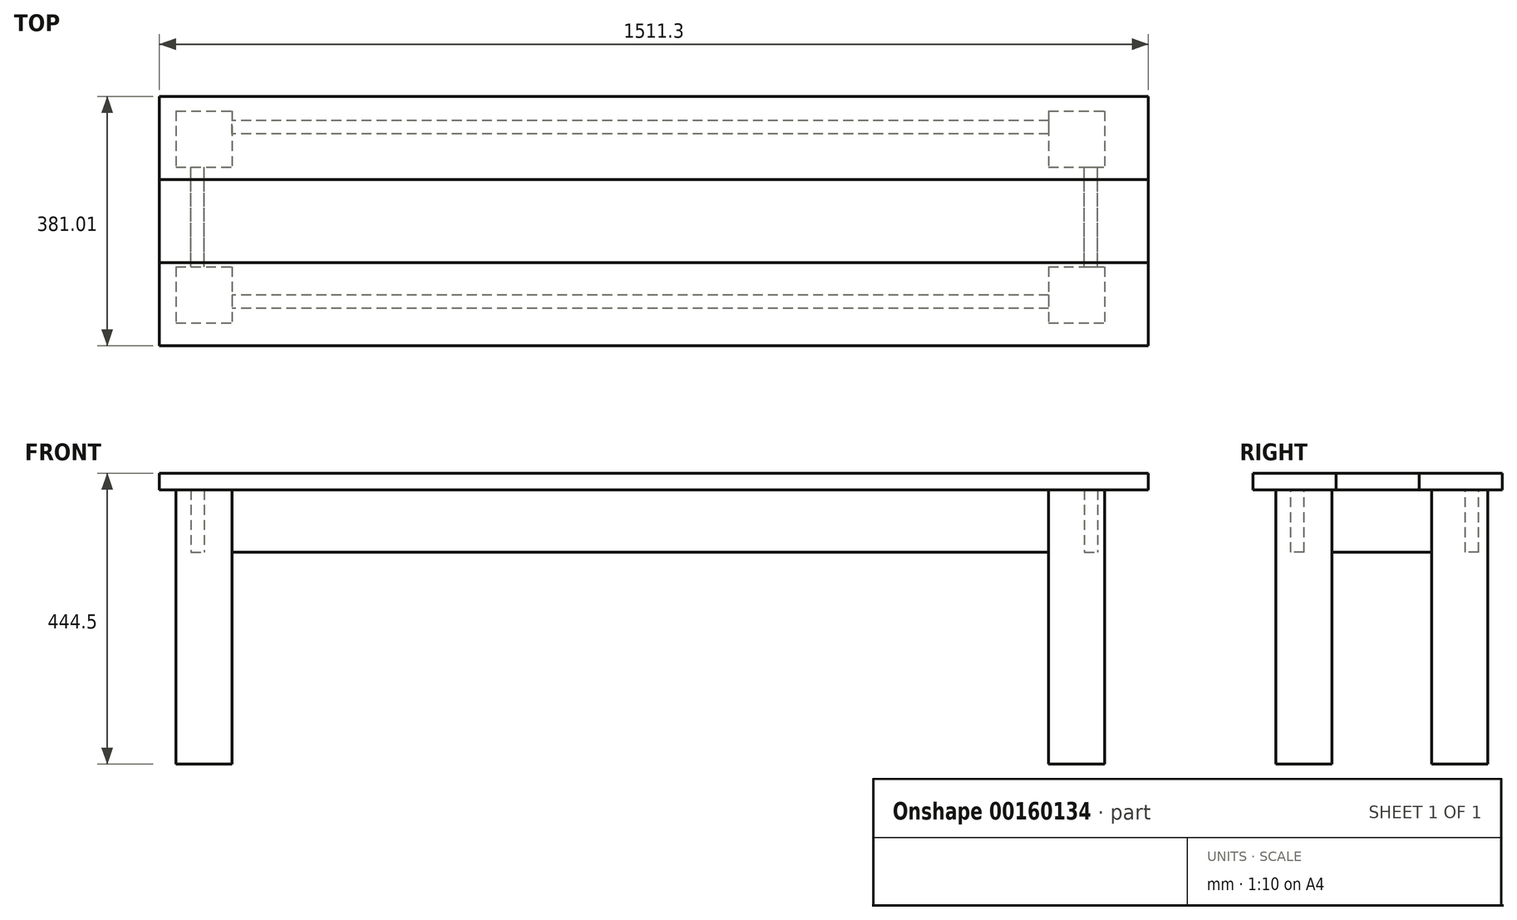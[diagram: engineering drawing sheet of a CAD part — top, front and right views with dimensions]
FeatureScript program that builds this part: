
annotation { "Feature Type Name" : "Feature", "Feature Type Description" : "" }
export const myFeature = defineFeature(function(context is Context, id is Id, definition is map)
    precondition{}
    {
        {
            var Q0;
            Q0=qCreatedBy(makeId("Top.planeOp"),FACE);
            var sketch = newSketch(context, id + "F0", { "sketchPlane" : qUnion([Q0])});
            skLineSegment(sketch, "E0.bottom", {"start": v(0, -127) * mm, "end": v(1511.3, -127) * mm});
            skLineSegment(sketch, "E0.top", {"start": v(0, 0) * mm, "end": v(1511.3, 0) * mm});
            skLineSegment(sketch, "E0.left", {"start": v(0, -127) * mm, "end": v(0, 0) * mm});
            skLineSegment(sketch, "E0.right", {"start": v(1511.3, -127) * mm, "end": v(1511.3, 0) * mm});
            skLineSegment(sketch, "E1.0.1.1", {"start": v(0, 127) * mm, "end": v(1511.3, 127) * mm});
            skLineSegment(sketch, "E1.0.1.2", {"start": v(0, 0) * mm, "end": v(0, 127) * mm});
            skLineSegment(sketch, "E1.0.1.3", {"start": v(1511.3, 0) * mm, "end": v(1511.3, 127) * mm});
            skLineSegment(sketch, "E1.0.2.0", {"start": v(0, 127) * mm, "end": v(1511.3, 127) * mm});
            skLineSegment(sketch, "E1.0.2.1", {"start": v(0, 254) * mm, "end": v(1511.3, 254) * mm});
            skLineSegment(sketch, "E1.0.2.2", {"start": v(0, 127) * mm, "end": v(0, 254) * mm});
            skLineSegment(sketch, "E1.0.2.3", {"start": v(1511.3, 127) * mm, "end": v(1511.3, 254) * mm});
            skLineSegment(sketch, "E1.direction1", {"start": v(0, -127) * mm, "end": v(25.4, -127) * mm, "construction": true});
            skLineSegment(sketch, "E1.direction2", {"start": v(0, -127) * mm, "end": v(0, 0) * mm, "construction": true});
            skSolve(sketch);
        }
        {
            var Q0;
            Q0=makeQuery(id+"F0.imprint","IMPRINT",FACE,{"disambiguationData":[TD([[makeQuery(id+"F0.imprint","IMPRINT",EDGE,{"derivedFrom":sQuery(id+"F0.wireOp",EDGE,"E0.bottom")}),1.0]])]});
            var sketch = newSketch(context, id + "F1", { "sketchPlane" : qUnion([Q0])});
            skLineSegment(sketch, "E2.bottom", {"start": v(25.4, 231.77) * mm, "end": v(111.13, 231.77) * mm});
            skLineSegment(sketch, "E2.top", {"start": v(25.4, 146.05) * mm, "end": v(111.13, 146.05) * mm});
            skLineSegment(sketch, "E2.left", {"start": v(25.4, 231.77) * mm, "end": v(25.4, 146.05) * mm});
            skLineSegment(sketch, "E2.right", {"start": v(111.12, 231.77) * mm, "end": v(111.12, 146.05) * mm});
            skLineSegment(sketch, "E3.0.1.0", {"start": v(25.4, -6.35) * mm, "end": v(111.12, -6.35) * mm});
            skLineSegment(sketch, "E3.0.1.1", {"start": v(25.4, -92.08) * mm, "end": v(111.12, -92.08) * mm});
            skLineSegment(sketch, "E3.0.1.2", {"start": v(25.4, -6.35) * mm, "end": v(25.4, -92.08) * mm});
            skLineSegment(sketch, "E3.0.1.3", {"start": v(111.12, -6.35) * mm, "end": v(111.12, -92.08) * mm});
            skLineSegment(sketch, "E3.1.0.0", {"start": v(1358.9, 231.77) * mm, "end": v(1444.62, 231.77) * mm});
            skLineSegment(sketch, "E3.1.0.1", {"start": v(1358.9, 146.05) * mm, "end": v(1444.62, 146.05) * mm});
            skLineSegment(sketch, "E3.1.0.2", {"start": v(1358.9, 231.77) * mm, "end": v(1358.9, 146.05) * mm});
            skLineSegment(sketch, "E3.1.0.3", {"start": v(1444.62, 231.77) * mm, "end": v(1444.62, 146.05) * mm});
            skLineSegment(sketch, "E3.1.1.0", {"start": v(1358.9, -6.35) * mm, "end": v(1444.62, -6.35) * mm});
            skLineSegment(sketch, "E3.1.1.1", {"start": v(1358.9, -92.08) * mm, "end": v(1444.62, -92.08) * mm});
            skLineSegment(sketch, "E3.1.1.2", {"start": v(1358.9, -6.35) * mm, "end": v(1358.9, -92.08) * mm});
            skLineSegment(sketch, "E3.1.1.3", {"start": v(1444.62, -6.35) * mm, "end": v(1444.62, -92.08) * mm});
            skLineSegment(sketch, "E3.direction1", {"start": v(25.4, 146.05) * mm, "end": v(1358.9, 146.05) * mm, "construction": true});
            skLineSegment(sketch, "E3.direction2", {"start": v(25.4, 146.05) * mm, "end": v(25.4, -92.08) * mm, "construction": true});
            skSolve(sketch);
        }
        {
            var Q0;
            Q0 = qSketchRegion(id + "F0", true);
            extrude(context, id + "F2", {"entities" : qUnion([Q0]), "depth" : 25.4 * mm});
        }
        {
            var Q0;
            Q0 = qSketchRegion(id + "F1", true);
            extrude(context, id + "F3", {"entities" : qUnion([Q0]), "oppositeDirection" : true, "offsetDistance" : 25.4 * mm, "depth" : 419.1 * mm});
        }
        {
            var Q0;
            Q0=makeQuery(id+"F3.opExtrude","SWEPT_FACE",FACE,{"disambiguationData":[OSD([sQuery(id+"F1.wireOp",EDGE,"E3.0.1.3")])]});
            var sketch = newSketch(context, id + "F4", { "sketchPlane" : qUnion([Q0])});
            skPoint(sketch, "E4.oppositeSnap0", {"position": v(-49.21, 0) * mm});
            skLineSegment(sketch, "E4.bottom", {"start": v(-69.53, 0) * mm, "end": v(-49.21, 0) * mm});
            skLineSegment(sketch, "E4.top", {"start": v(-69.53, -95.25) * mm, "end": v(-49.21, -95.25) * mm});
            skLineSegment(sketch, "E4.left", {"start": v(-69.53, 0) * mm, "end": v(-69.53, -95.25) * mm});
            skLineSegment(sketch, "E4.right", {"start": v(-49.21, 0) * mm, "end": v(-49.21, -95.25) * mm});
            skPoint(sketch, "E5.1.0.0", {"position": v(217.49, 0) * mm});
            skLineSegment(sketch, "E5.1.0.1", {"start": v(217.49, 0) * mm, "end": v(217.49, -95.25) * mm});
            skLineSegment(sketch, "E5.1.0.2", {"start": v(197.17, 0) * mm, "end": v(197.17, -95.25) * mm});
            skLineSegment(sketch, "E5.1.0.3", {"start": v(197.17, -95.25) * mm, "end": v(217.49, -95.25) * mm});
            skLineSegment(sketch, "E5.1.0.4", {"start": v(197.17, 0) * mm, "end": v(217.49, 0) * mm});
            skLineSegment(sketch, "E5.direction1", {"start": v(-69.53, -95.25) * mm, "end": v(197.17, -95.25) * mm, "construction": true});
            skSolve(sketch);
        }
        {
            var Q0;
            Q0 = qSketchRegion(id + "F4", true);
            var Q1;
            Q1=makeQuery(id+"F3.opExtrude","SWEPT_FACE",FACE,{"disambiguationData":[OSD([sQuery(id+"F1.wireOp",EDGE,"E3.1.0.2")])]});
            extrude(context, id + "F5", {"entities" : qUnion([Q0]), "endBound" : BoundingType.UP_TO_SURFACE, "endBoundEntityFace" : qUnion([Q1]), "depth" : 25.4 * mm});
        }
        {
            var Q0;
            Q0=makeQuery(id+"F3.opExtrude","SWEPT_FACE",FACE,{"disambiguationData":[OSD([sQuery(id+"F1.wireOp",EDGE,"E2.top")])]});
            var sketch = newSketch(context, id + "F6", { "sketchPlane" : qUnion([Q0])});
            skPoint(sketch, "E6.oppositeSnap0", {"position": v(68.26, 0) * mm});
            skLineSegment(sketch, "E6.bottom", {"start": v(47.94, 0) * mm, "end": v(68.26, 0) * mm});
            skLineSegment(sketch, "E6.top", {"start": v(47.94, -95.25) * mm, "end": v(68.26, -95.25) * mm});
            skLineSegment(sketch, "E6.left", {"start": v(47.94, 0) * mm, "end": v(47.94, -95.25) * mm});
            skLineSegment(sketch, "E6.right", {"start": v(68.26, 0) * mm, "end": v(68.26, -95.25) * mm});
            skPoint(sketch, "E7.1.0.0", {"position": v(1433.51, 0) * mm});
            skLineSegment(sketch, "E7.1.0.1", {"start": v(1413.2, 0) * mm, "end": v(1433.51, 0) * mm});
            skLineSegment(sketch, "E7.1.0.2", {"start": v(1413.2, -95.25) * mm, "end": v(1433.51, -95.25) * mm});
            skLineSegment(sketch, "E7.1.0.3", {"start": v(1413.2, 0) * mm, "end": v(1413.2, -95.25) * mm});
            skLineSegment(sketch, "E7.1.0.4", {"start": v(1433.51, 0) * mm, "end": v(1433.51, -95.25) * mm});
            skLineSegment(sketch, "E7.direction1", {"start": v(47.94, -95.25) * mm, "end": v(1413.2, -95.25) * mm, "construction": true});
            skSolve(sketch);
        }
        {
            var Q0;
            Q0 = qSketchRegion(id + "F6", true);
            var Q1;
            Q1=makeQuery(id+"F3.opExtrude","SWEPT_FACE",FACE,{"disambiguationData":[OSD([sQuery(id+"F1.wireOp",EDGE,"E3.0.1.0")])]});
            var Q2;
            Q2=makeQuery(id+"F3.opExtrude","SWEPT_BODY",BODY,{"disambiguationData":[OSD([sQuery(id+"F1.wireOp",EDGE,"E3.0.1.0"),sQuery(id+"F1.wireOp",EDGE,"E3.0.1.1"),sQuery(id+"F1.wireOp",EDGE,"E3.0.1.2"),sQuery(id+"F1.wireOp",EDGE,"E3.0.1.3")])]});
            extrude(context, id + "F7", {"entities" : qUnion([Q0]), "endBoundEntityFace" : qUnion([Q1]), "endBoundEntityBody" : qUnion([Q2]), "depth" : 152.4 * mm});
        }
    });
